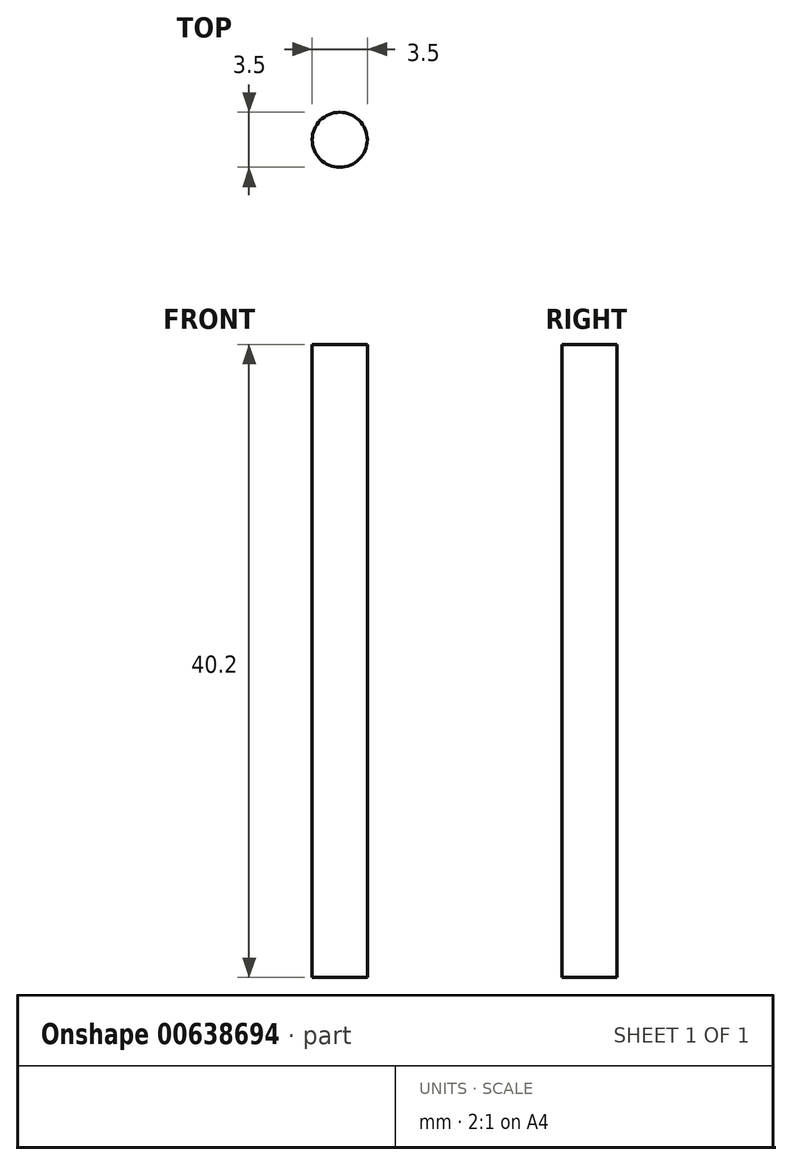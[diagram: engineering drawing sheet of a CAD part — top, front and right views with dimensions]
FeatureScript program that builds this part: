
annotation { "Feature Type Name" : "Feature", "Feature Type Description" : "" }
export const myFeature = defineFeature(function(context is Context, id is Id, definition is map)
    precondition{}
    {
        {
            var Q0;
            Q0=qCreatedBy(makeId("Top.planeOp"),FACE);
            var sketch = newSketch(context, id + "F0", { "sketchPlane" : qUnion([Q0])});
            skCircle(sketch, "E0", {"center": v(0, 0) * mm, "radius": 1.75 * mm});
            skSolve(sketch);
        }
        {
            var Q0;
            Q0=makeQuery(id+"F0.imprint","IMPRINT",FACE,{"disambiguationData":[TD([[makeQuery(id+"F0.imprint","IMPRINT",EDGE,{"derivedFrom":sQuery(id+"F0.wireOp",EDGE,"E0")}),1.0]])]});
            extrude(context, id + "F1", {"entities" : qUnion([Q0]), "depth" : 40.2 * mm, "offsetDistance" : 25 * mm});
        }
    });
